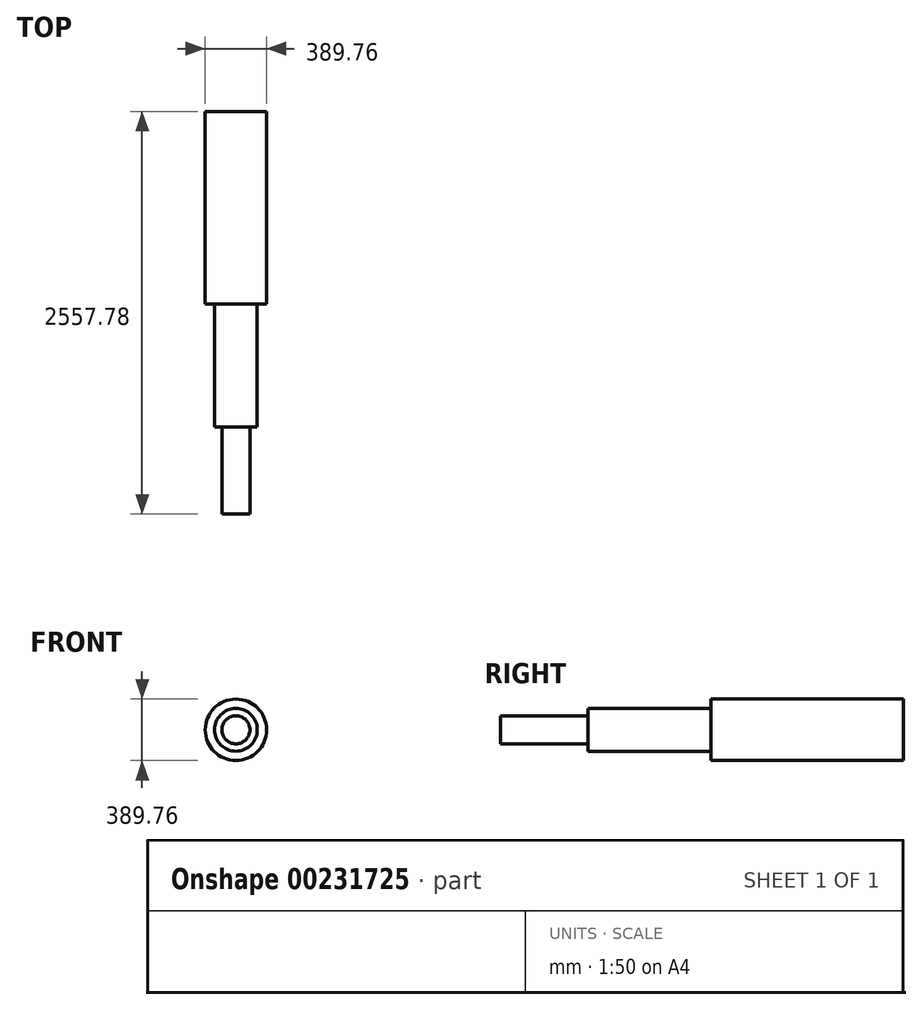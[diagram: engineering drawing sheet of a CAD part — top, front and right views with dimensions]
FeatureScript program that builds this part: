
annotation { "Feature Type Name" : "Feature", "Feature Type Description" : "" }
export const myFeature = defineFeature(function(context is Context, id is Id, definition is map)
    precondition{}
    {
        {
            var Q0;
            Q0=qCreatedBy(makeId("Front.planeOp"),FACE);
            var sketch = newSketch(context, id + "F0", { "sketchPlane" : qUnion([Q0])});
            skCircle(sketch, "E0", {"center": v(0, 0) * mm, "radius": 194.88 * mm});
            skSolve(sketch);
        }
        {
            var Q0;
            Q0=makeQuery(id+"F0.imprint","IMPRINT",FACE,{"disambiguationData":[TD([[makeQuery(id+"F0.imprint","IMPRINT",EDGE,{"derivedFrom":sQuery(id+"F0.wireOp",EDGE,"E0")}),1.0]])]});
            extrude(context, id + "F1", {"entities" : qUnion([Q0]), "depth" : 1221.74 * mm});
        }
        {
            var Q0;
            Q0=makeQuery(id+"F1.opExtrude","CAP_FACE",FACE,{"disambiguationData":[OSD([sQuery(id+"F0.wireOp",EDGE,"E0")])],"isStart":false});
            var sketch = newSketch(context, id + "F2", { "sketchPlane" : qUnion([Q0])});
            skCircle(sketch, "E1", {"center": v(0, 0) * mm, "radius": 135.76 * mm});
            skSolve(sketch);
        }
        {
            var Q0;
            Q0=makeQuery(id+"F2.imprint","IMPRINT",FACE,{"disambiguationData":[TD([[makeQuery(id+"F2.imprint","IMPRINT",EDGE,{"derivedFrom":sQuery(id+"F2.wireOp",EDGE,"E1")}),1.0]])]});
            extrude(context, id + "F3", {"entities" : qUnion([Q0]), "depth" : 781.56 * mm});
        }
        {
            var Q0;
            Q0=makeQuery(id+"F3.opExtrude","CAP_FACE",FACE,{"disambiguationData":[OSD([sQuery(id+"F2.wireOp",EDGE,"E1")])],"isStart":false});
            var sketch = newSketch(context, id + "F4", { "sketchPlane" : qUnion([Q0])});
            skCircle(sketch, "E2", {"center": v(0, 0) * mm, "radius": 88.9 * mm});
            skSolve(sketch);
        }
        {
            var Q0;
            Q0=makeQuery(id+"F4.imprint","IMPRINT",FACE,{"disambiguationData":[TD([[makeQuery(id+"F4.imprint","IMPRINT",EDGE,{"derivedFrom":sQuery(id+"F4.wireOp",EDGE,"E2")}),1.0]])]});
            extrude(context, id + "F5", {"entities" : qUnion([Q0]), "operationType" : NewBodyOperationType.ADD, "depth" : 554.48 * mm});
        }
    });
